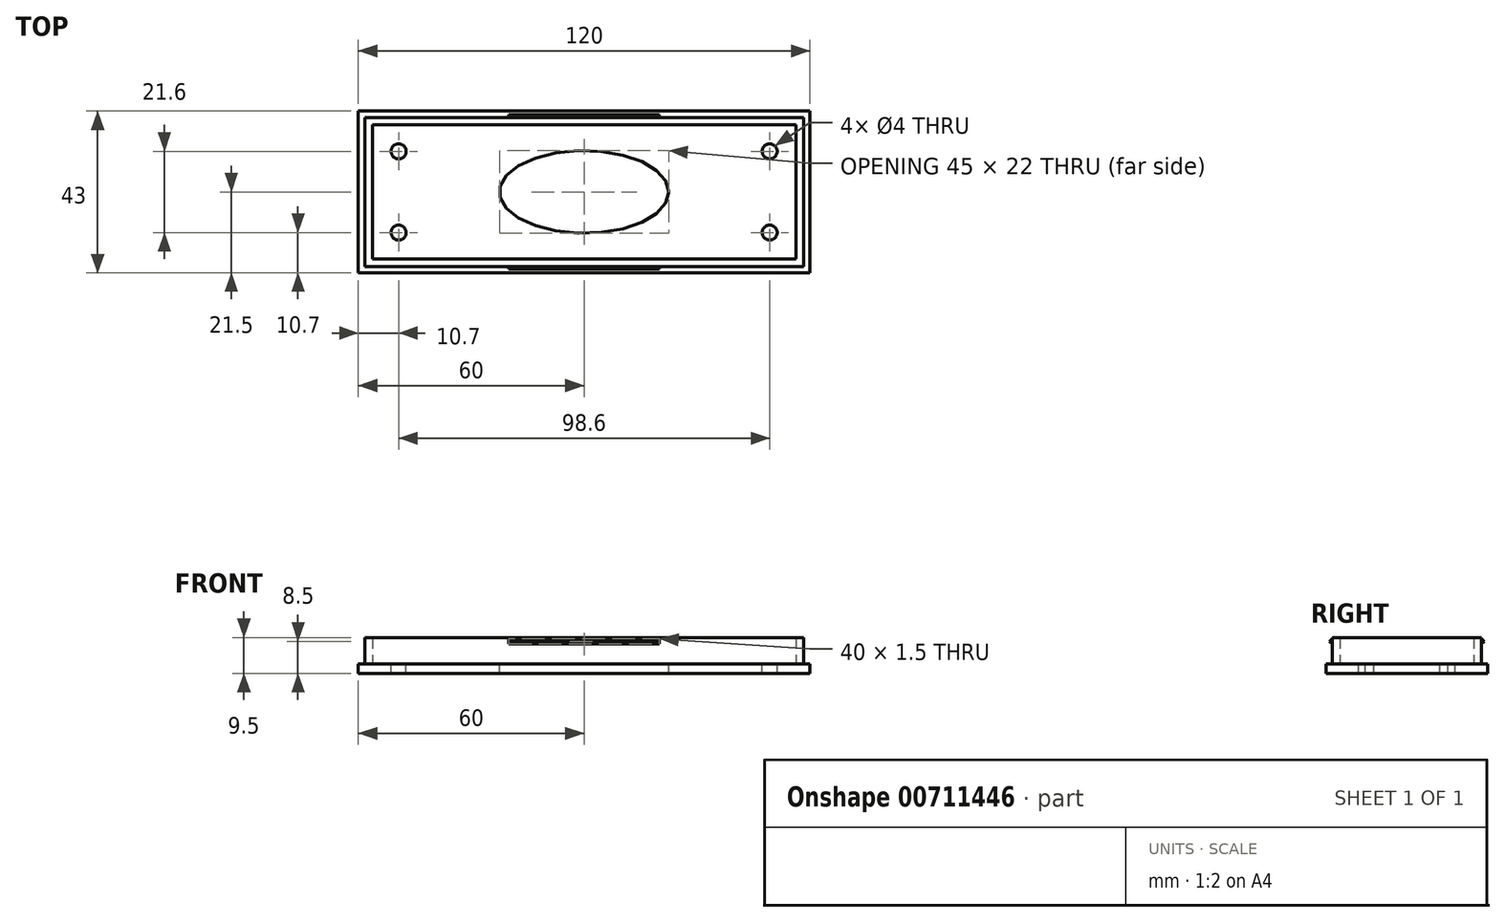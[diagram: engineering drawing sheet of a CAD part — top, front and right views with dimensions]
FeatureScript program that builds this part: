
annotation { "Feature Type Name" : "Feature", "Feature Type Description" : "" }
export const myFeature = defineFeature(function(context is Context, id is Id, definition is map)
    precondition{}
    {
        {
            var Q0;
            Q0=qCreatedBy(makeId("Top.planeOp"),FACE);
            var sketch = newSketch(context, id + "F0", { "sketchPlane" : qUnion([Q0])});
            skLineSegment(sketch, "E0.bottom", {"start": v(60, 21.5) * mm, "end": v(-60, 21.5) * mm});
            skLineSegment(sketch, "E0.top", {"start": v(60, -21.5) * mm, "end": v(-60, -21.5) * mm});
            skLineSegment(sketch, "E0.left", {"start": v(60, 21.5) * mm, "end": v(60, -21.5) * mm});
            skLineSegment(sketch, "E0.right", {"start": v(-60, 21.5) * mm, "end": v(-60, -21.5) * mm});
            skPoint(sketch, "E0.middle", {"position": v(0, 0) * mm});
            skLineSegment(sketch, "E1.0", {"start": v(58.3, 19.8) * mm, "end": v(-58.3, 19.8) * mm});
            skLineSegment(sketch, "E1.1", {"start": v(58.3, 19.8) * mm, "end": v(58.3, -19.8) * mm});
            skLineSegment(sketch, "E1.2", {"start": v(58.3, -19.8) * mm, "end": v(-58.3, -19.8) * mm});
            skLineSegment(sketch, "E1.3", {"start": v(-58.3, 19.8) * mm, "end": v(-58.3, -19.8) * mm});
            skLineSegment(sketch, "E2.0", {"start": v(56.3, 17.8) * mm, "end": v(-56.3, 17.8) * mm});
            skLineSegment(sketch, "E2.1", {"start": v(56.3, 17.8) * mm, "end": v(56.3, -17.8) * mm});
            skLineSegment(sketch, "E2.2", {"start": v(56.3, -17.8) * mm, "end": v(-56.3, -17.8) * mm});
            skLineSegment(sketch, "E2.3", {"start": v(-56.3, 17.8) * mm, "end": v(-56.3, -17.8) * mm});
            skCircle(sketch, "E3", {"center": v(-49.3, 10.8) * mm, "radius": 2 * mm});
            skCircle(sketch, "E4", {"center": v(-49.3, -10.8) * mm, "radius": 2 * mm});
            skCircle(sketch, "E5", {"center": v(49.3, 10.8) * mm, "radius": 2 * mm});
            skCircle(sketch, "E6", {"center": v(49.3, -10.8) * mm, "radius": 2 * mm});
            skEllipse(sketch, "E7", {"center": v(0, 0) * mm, "majorRadius": 22.5 * mm, "minorRadius": 11 * mm, "majorAxis": v(1, 0)});
            skLineSegment(sketch, "E8", {"start": v(0, 17.8) * mm, "end": v(0, -17.8) * mm, "construction": true});
            skLineSegment(sketch, "E9", {"start": v(-56.3, 0) * mm, "end": v(56.3, 0) * mm, "construction": true});
            skSolve(sketch);
        }
        {
            var Q0;
            Q0=makeQuery(id+"F0.imprint","IMPRINT",FACE,{"disambiguationData":[TD([[makeQuery(id+"F0.imprint","IMPRINT",EDGE,{"derivedFrom":sQuery(id+"F0.wireOp",EDGE,"E0.bottom")}),1.0]])]});
            var Q1;
            Q1=makeQuery(id+"F0.imprint","IMPRINT",FACE,{"disambiguationData":[TD([[makeQuery(id+"F0.imprint","IMPRINT",EDGE,{"derivedFrom":sQuery(id+"F0.wireOp",EDGE,"E1.0")}),1.0]])]});
            var Q2;
            Q2=makeQuery(id+"F0.imprint","IMPRINT",FACE,{"disambiguationData":[TD([[makeQuery(id+"F0.imprint","IMPRINT",EDGE,{"derivedFrom":sQuery(id+"F0.wireOp",EDGE,"E2.0")}),1.0]])]});
            extrude(context, id + "F1", {"entities" : qUnion([Q0, Q1, Q2]), "oppositeDirection" : true, "depth" : 2.5 * mm, "offsetDistance" : 25 * mm});
        }
        {
            var Q0;
            Q0=makeQuery(id+"F0.imprint","IMPRINT",FACE,{"disambiguationData":[TD([[makeQuery(id+"F0.imprint","IMPRINT",EDGE,{"derivedFrom":sQuery(id+"F0.wireOp",EDGE,"E1.0")}),1.0]])]});
            extrude(context, id + "F2", {"entities" : qUnion([Q0]), "operationType" : NewBodyOperationType.ADD, "depth" : 7 * mm, "offsetDistance" : 25 * mm});
        }
        {
            var Q0;
            Q0=makeQuery(id+"F2.opExtrude","SWEPT_FACE",FACE,{"disambiguationData":[OSD([sQuery(id+"F0.wireOp",EDGE,"E1.0")])]});
            var sketch = newSketch(context, id + "F3", { "sketchPlane" : qUnion([Q0])});
            skLineSegment(sketch, "E10", {"start": v(-58.3, 6) * mm, "end": v(58.3, 6) * mm, "construction": true});
            skLineSegment(sketch, "E11.bottom", {"start": v(20, 5.25) * mm, "end": v(-20, 5.25) * mm});
            skLineSegment(sketch, "E11.top", {"start": v(20, 6.75) * mm, "end": v(-20, 6.75) * mm});
            skLineSegment(sketch, "E11.left", {"start": v(20, 5.25) * mm, "end": v(20, 6.75) * mm});
            skLineSegment(sketch, "E11.right", {"start": v(-20, 5.25) * mm, "end": v(-20, 6.75) * mm});
            skPoint(sketch, "E11.middle", {"position": v(0, 6) * mm});
            skSolve(sketch);
        }
        {
            var Q0;
            Q0 = qSketchRegion(id + "F3", true);
            extrude(context, id + "F4", {"entities" : qUnion([Q0]), "depth" : 0.8 * mm, "offsetDistance" : 25 * mm});
        }
        {
            var Q0;
            Q0=makeQuery(id+"F4.opExtrude","CAP_EDGE",EDGE,{"disambiguationData":[OSD([sQuery(id+"F3.wireOp",EDGE,"E11.bottom")])],"isStart":false});
            var Q1;
            Q1=makeQuery(id+"F4.opExtrude","CAP_EDGE",EDGE,{"disambiguationData":[OSD([sQuery(id+"F3.wireOp",EDGE,"E11.top")])],"isStart":false});
            chamfer(context, id + "F5", {"entities" : qUnion([Q0, Q1]), "width" : 0.8 * mm, "tangentPropagation" : true});
        }
        {
            var Q0;
            Q0=makeQuery(id+"F4.opExtrude","SWEPT_BODY",BODY,{"disambiguationData":[OSD([sQuery(id+"F3.wireOp",EDGE,"E11.bottom"),sQuery(id+"F3.wireOp",EDGE,"E11.top"),sQuery(id+"F3.wireOp",EDGE,"E11.left"),sQuery(id+"F3.wireOp",EDGE,"E11.right")])]});
            var Q1;
            Q1=qCreatedBy(makeId("Front.planeOp"),FACE);
            mirror(context, id + "F6", {"operationType" : NewBodyOperationType.ADD, "entities" : qUnion([Q0]), "mirrorPlane" : qUnion([Q1])});
        }
    });
